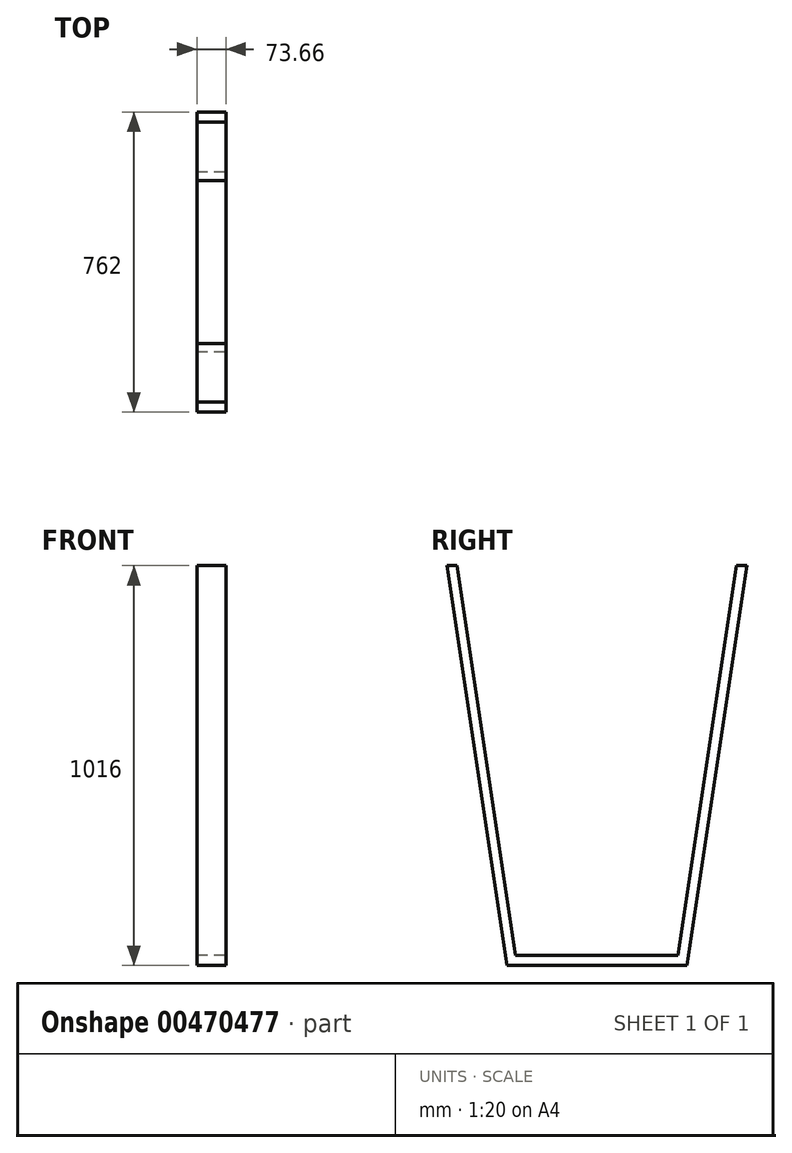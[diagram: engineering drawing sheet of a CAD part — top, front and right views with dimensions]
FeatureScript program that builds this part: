
annotation { "Feature Type Name" : "Feature", "Feature Type Description" : "" }
export const myFeature = defineFeature(function(context is Context, id is Id, definition is map)
    precondition{}
    {
        {
            var Q0;
            Q0=qCreatedBy(makeId("Right.planeOp"),FACE);
            var sketch = newSketch(context, id + "F0", { "sketchPlane" : qUnion([Q0])});
            skLineSegment(sketch, "E0", {"start": v(0, 0) * mm, "end": v(228.6, 0) * mm});
            skLineSegment(sketch, "E1", {"start": v(228.6, 0) * mm, "end": v(381, 1016) * mm});
            skLineSegment(sketch, "E2.0", {"start": v(206.73, 25.4) * mm, "end": v(355.32, 1016) * mm});
            skLineSegment(sketch, "E2.1", {"start": v(0, 25.4) * mm, "end": v(206.73, 25.4) * mm});
            skLineSegment(sketch, "E3", {"start": v(381, 1016) * mm, "end": v(355.32, 1016) * mm});
            skLineSegment(sketch, "E4.MirrorCS", {"start": v(-206.73, 25.4) * mm, "end": v(-355.32, 1016) * mm});
            skLineSegment(sketch, "E5.MirrorCS", {"start": v(-228.6, 0) * mm, "end": v(-381, 1016) * mm});
            skLineSegment(sketch, "E6.MirrorCS", {"start": v(-381, 1016) * mm, "end": v(-355.32, 1016) * mm});
            skLineSegment(sketch, "E7.MirrorCS", {"start": v(0, 0) * mm, "end": v(-228.6, 0) * mm});
            skLineSegment(sketch, "E8.MirrorCS", {"start": v(0, 25.4) * mm, "end": v(-206.73, 25.4) * mm});
            skSolve(sketch);
        }
        {
            var Q0;
            Q0 = qSketchRegion(id + "F0", true);
            extrude(context, id + "F1", {"entities" : qUnion([Q0]), "depth" : 73.66 * mm});
        }
    });
